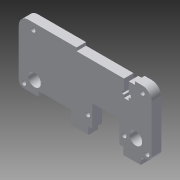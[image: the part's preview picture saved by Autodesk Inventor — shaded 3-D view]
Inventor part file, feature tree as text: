
AUTODESK INVENTOR PART (.ipt)
format: ipt  version: 2013 (Build 170138000, 138)  size: 139,264 bytes
history: native  units: mm
features: extrude x1, sketch x1
ambient origin geometry x8: Origin, YZ Plane, XZ Plane, XY Plane, X Axis, Y Axis, Z Axis, Center Point
bodies: Solid1 (feature_tree)
feature tree (2):
  extrude  "Extrusion1"  [1 undecoded]
  sketch  "Sketch1"  dims[d0=6.0mm d1=0.0mm]
note: 1 required parameter value undecoded (feature->parameter linkage not recoverable at this tier; creation-order binding heuristic only, values carry confidence <= 0.55)
